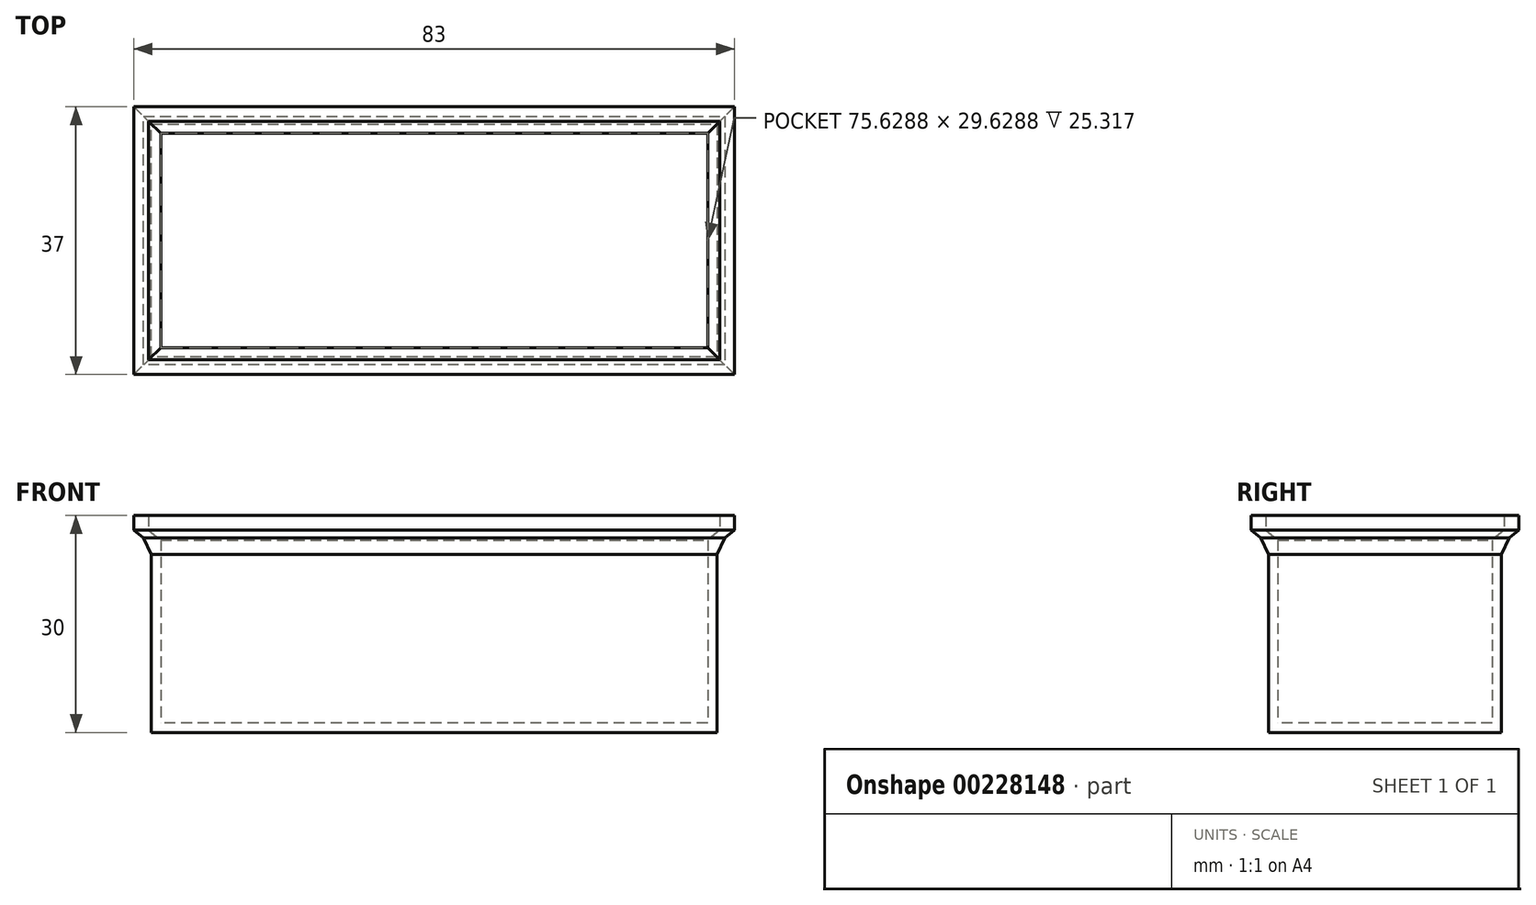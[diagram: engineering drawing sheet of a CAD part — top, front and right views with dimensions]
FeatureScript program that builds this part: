
annotation { "Feature Type Name" : "Feature", "Feature Type Description" : "" }
export const myFeature = defineFeature(function(context is Context, id is Id, definition is map)
    precondition{}
    {
        {
            assignVariable(context, id + "F0", {"name" : "Height", "anyValue" : 30});
        }
        {
            assignVariable(context, id + "F1", {"name" : "WallThickness", "anyValue" : 2});
        }
        {
            var Q0;
            Q0=qCreatedBy(makeId("Top.planeOp"),FACE);
            var sketch = newSketch(context, id + "F2", { "sketchPlane" : qUnion([Q0])});
            skLineSegment(sketch, "E0.bottom", {"start": v(39.1, 16.1) * mm, "end": v(-39.1, 16.1) * mm});
            skLineSegment(sketch, "E0.top", {"start": v(39.1, -16.1) * mm, "end": v(-39.1, -16.1) * mm});
            skLineSegment(sketch, "E0.left", {"start": v(39.1, 16.1) * mm, "end": v(39.1, -16.1) * mm});
            skLineSegment(sketch, "E0.right", {"start": v(-39.1, 16.1) * mm, "end": v(-39.1, -16.1) * mm});
            skPoint(sketch, "E0.middle", {"position": v(0, 0) * mm});
            skSolve(sketch);
        }
        {
            var Q0;
            Q0=makeQuery(id+"F2.imprint","IMPRINT",FACE,{"disambiguationData":[TD([[makeQuery(id+"F2.imprint","IMPRINT",EDGE,{"derivedFrom":sQuery(id+"F2.wireOp",EDGE,"E0.bottom")}),1.0]])]});
            extrude(context, id + "F3", {"entities" : qUnion([Q0]), "depth" : (getVariable(context, 'Height') - 4) * mm});
        }
        {
            var Q0;
            Q0=makeQuery(id+"F3.opExtrude","CAP_FACE",FACE,{"disambiguationData":[OSD([sQuery(id+"F2.wireOp",EDGE,"E0.bottom"),sQuery(id+"F2.wireOp",EDGE,"E0.top"),sQuery(id+"F2.wireOp",EDGE,"E0.left"),sQuery(id+"F2.wireOp",EDGE,"E0.right")])],"isStart":false});
            cPlane(context, id + "F4", {"entities" : qUnion([Q0]), "cplaneType" : CPlaneType.OFFSET, "offset" : (getVariable(context, 'WallThickness')) * mm, "width" : 150 * mm, "height" : 150 * mm});
        }
        {
            var Q0;
            Q0=qCreatedBy(id+"F4.planeOp",FACE);
            var sketch = newSketch(context, id + "F5", { "sketchPlane" : qUnion([Q0])});
            skLineSegment(sketch, "E1.0.0", {"start": v(-39.1, -16.1) * mm, "end": v(39.1, -16.1) * mm, "construction": true});
            skLineSegment(sketch, "E1.0.1", {"start": v(39.1, -16.1) * mm, "end": v(39.1, 16.1) * mm, "construction": true});
            skLineSegment(sketch, "E1.0.2", {"start": v(39.1, 16.1) * mm, "end": v(-39.1, 16.1) * mm, "construction": true});
            skLineSegment(sketch, "E1.0.3", {"start": v(-39.1, 16.1) * mm, "end": v(-39.1, -16.1) * mm, "construction": true});
            skLineSegment(sketch, "E2.0", {"start": v(-39.5, 16.5) * mm, "end": v(-39.5, -16.5) * mm, "construction": true});
            skLineSegment(sketch, "E2.1", {"start": v(39.5, 16.5) * mm, "end": v(-39.5, 16.5) * mm, "construction": true});
            skLineSegment(sketch, "E2.2", {"start": v(39.5, -16.5) * mm, "end": v(39.5, 16.5) * mm, "construction": true});
            skLineSegment(sketch, "E2.3", {"start": v(-39.5, -16.5) * mm, "end": v(39.5, -16.5) * mm, "construction": true});
            skLineSegment(sketch, "E3.0", {"start": v(-41.5, 18.5) * mm, "end": v(-41.5, -18.5) * mm});
            skLineSegment(sketch, "E3.1", {"start": v(41.5, 18.5) * mm, "end": v(-41.5, 18.5) * mm});
            skLineSegment(sketch, "E3.2", {"start": v(41.5, -18.5) * mm, "end": v(41.5, 18.5) * mm});
            skLineSegment(sketch, "E3.3", {"start": v(-41.5, -18.5) * mm, "end": v(41.5, -18.5) * mm});
            skSolve(sketch);
        }
        {
            var Q1;
            Q1=makeQuery(id+"F5.imprint","IMPRINT",FACE,{"disambiguationData":[TD([[makeQuery(id+"F5.imprint","IMPRINT",EDGE,{"derivedFrom":sQuery(id+"F5.wireOp",EDGE,"E3.0")}),1.0]])]});
            var Q2;
            Q2=makeQuery(id+"F3.opExtrude","CAP_FACE",FACE,{"disambiguationData":[OSD([sQuery(id+"F2.wireOp",EDGE,"E0.bottom"),sQuery(id+"F2.wireOp",EDGE,"E0.top"),sQuery(id+"F2.wireOp",EDGE,"E0.left"),sQuery(id+"F2.wireOp",EDGE,"E0.right")])],"isStart":false});
            loft(context, id + "F6", {"operationType" : NewBodyOperationType.ADD, "sheetProfilesArray" : [{ "sheetProfileEntities" : qUnion([Q1]) }, { "sheetProfileEntities" : qUnion([Q2]) }]});
        }
        {
            var Q0;
            Q0=makeQuery(id+"F6.opLoft","CAP_FACE",FACE,{"disambiguationData":[OSD([makeQuery(id+"F5.imprint","IMPRINT",FACE,{"disambiguationData":[TD([[makeQuery(id+"F5.imprint","IMPRINT",EDGE,{"derivedFrom":sQuery(id+"F5.wireOp",EDGE,"E3.0")}),1.0]])]})])],"isStart":true});
            shell(context, id + "F7", {"entities" : qUnion([Q0]), "thickness" : (getVariable(context, 'WallThickness') * cos(50 * degree)) * mm});
        }
        {
            var Q0;
            Q0=makeQuery(id+"F6.opLoft","CAP_FACE",FACE,{"disambiguationData":[OSD([makeQuery(id+"F5.imprint","IMPRINT",FACE,{"disambiguationData":[TD([[makeQuery(id+"F5.imprint","IMPRINT",EDGE,{"derivedFrom":sQuery(id+"F5.wireOp",EDGE,"E3.0")}),1.0]])]})])],"isStart":true});
            extrude(context, id + "F8", {"entities" : qUnion([Q0]), "operationType" : NewBodyOperationType.ADD, "depth" : (getVariable(context, 'WallThickness')) * mm});
        }
        {
            var Q0;
            {var subQ0=sQuery(id+"F2.wireOp",EDGE,"E0.right");Q0=makeQuery(id+"F6.boolean.opBoolean","MERGE",EDGE,{"derivedFrom":[makeQuery(id+"F3.opExtrude","CAP_EDGE",EDGE,{"disambiguationData":[OSD([subQ0])],"isStart":false}),makeQuery(id+"F6.opLoft","MID_CAP_EDGE",EDGE,{"disambiguationData":[OSD([sQuery(id+"F2.wireOp",EDGE,"E0.bottom"),sQuery(id+"F2.wireOp",EDGE,"E0.top"),subQ0])],"capPos":1.0})]});}
            var Q1;
            {var subQ0=sQuery(id+"F2.wireOp",EDGE,"E0.top");Q1=makeQuery(id+"F6.boolean.opBoolean","MERGE",EDGE,{"derivedFrom":[makeQuery(id+"F3.opExtrude","CAP_EDGE",EDGE,{"disambiguationData":[OSD([subQ0])],"isStart":false}),makeQuery(id+"F6.opLoft","MID_CAP_EDGE",EDGE,{"disambiguationData":[OSD([subQ0,sQuery(id+"F2.wireOp",EDGE,"E0.left"),sQuery(id+"F2.wireOp",EDGE,"E0.right")])],"capPos":1.0})]});}
            var Q2;
            {var subQ0=sQuery(id+"F2.wireOp",EDGE,"E0.left");Q2=makeQuery(id+"F6.boolean.opBoolean","MERGE",EDGE,{"derivedFrom":[makeQuery(id+"F3.opExtrude","CAP_EDGE",EDGE,{"disambiguationData":[OSD([subQ0])],"isStart":false}),makeQuery(id+"F6.opLoft","MID_CAP_EDGE",EDGE,{"disambiguationData":[OSD([sQuery(id+"F2.wireOp",EDGE,"E0.bottom"),sQuery(id+"F2.wireOp",EDGE,"E0.top"),subQ0])],"capPos":1.0})]});}
            var Q3;
            {var subQ0=sQuery(id+"F2.wireOp",EDGE,"E0.bottom");Q3=makeQuery(id+"F6.boolean.opBoolean","MERGE",EDGE,{"derivedFrom":[makeQuery(id+"F3.opExtrude","CAP_EDGE",EDGE,{"disambiguationData":[OSD([subQ0])],"isStart":false}),makeQuery(id+"F6.opLoft","MID_CAP_EDGE",EDGE,{"disambiguationData":[OSD([subQ0,sQuery(id+"F2.wireOp",EDGE,"E0.left"),sQuery(id+"F2.wireOp",EDGE,"E0.right")])],"capPos":1.0})]});}
            chamfer(context, id + "F9", {"entities" : qUnion([Q0, Q1, Q2, Q3]), "width" : 3 * mm, "tangentPropagation" : true});
        }
    });
